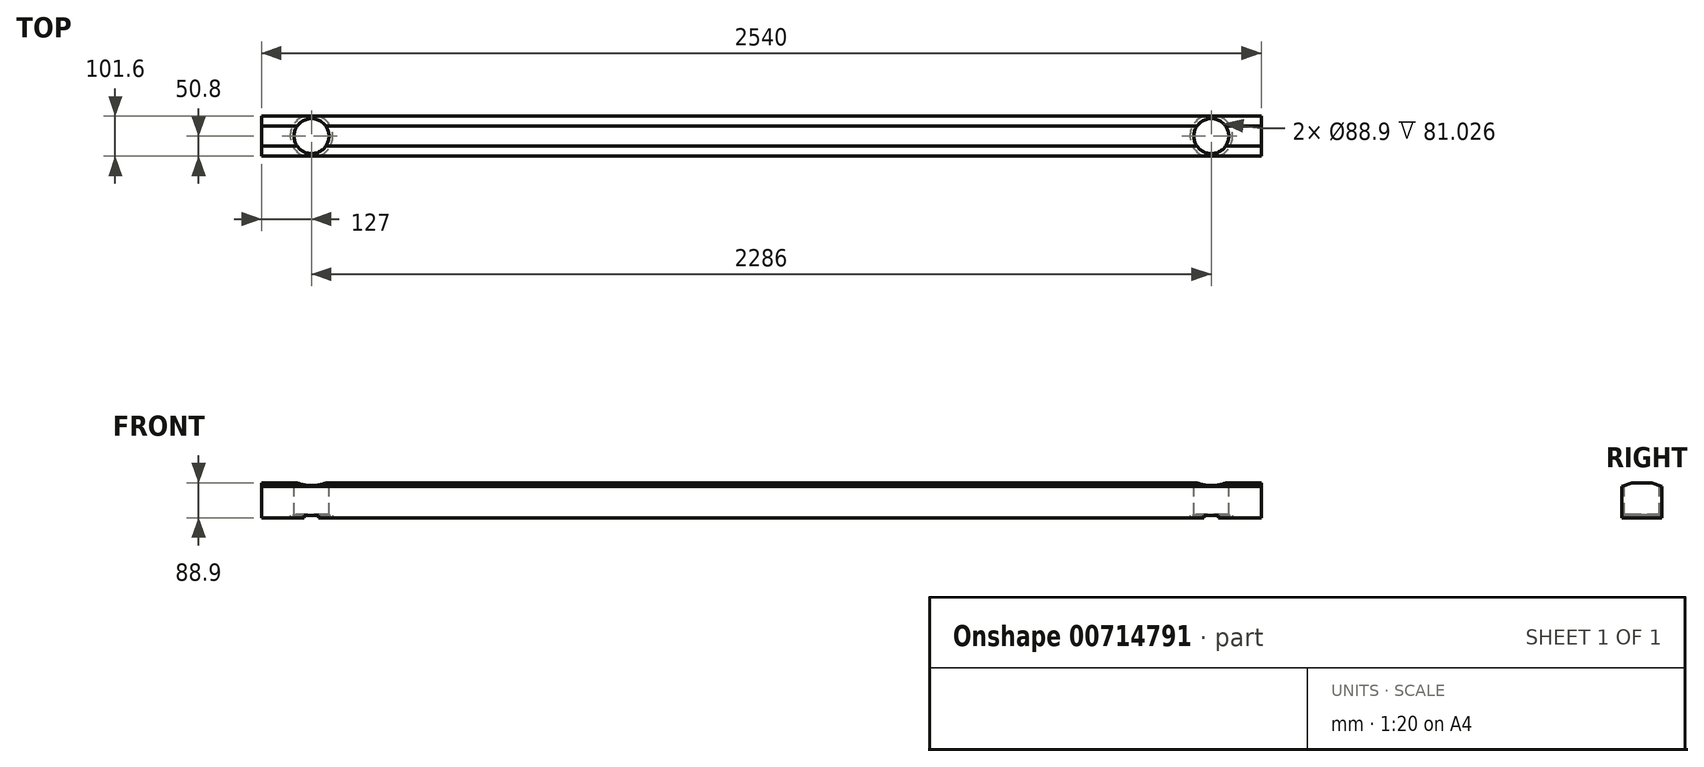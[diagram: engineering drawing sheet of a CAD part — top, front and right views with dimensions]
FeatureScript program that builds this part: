
annotation { "Feature Type Name" : "Feature", "Feature Type Description" : "" }
export const myFeature = defineFeature(function(context is Context, id is Id, definition is map)
    precondition{}
    {
        {
            var Q0;
            Q0=qCreatedBy(makeId("Right.planeOp"),FACE);
            var sketch = newSketch(context, id + "F0", { "sketchPlane" : qUnion([Q0])});
            skLineSegment(sketch, "E0", {"start": v(-25.4, 0) * mm, "end": v(25.4, 0) * mm});
            skLineSegment(sketch, "E1", {"start": v(25.4, 0) * mm, "end": v(50.8, -9.24) * mm});
            skLineSegment(sketch, "E2", {"start": v(-25.4, 0) * mm, "end": v(-50.8, -9.24) * mm});
            skLineSegment(sketch, "E3", {"start": v(-50.8, -9.24) * mm, "end": v(-50.8, -88.9) * mm});
            skLineSegment(sketch, "E4", {"start": v(-50.8, -88.9) * mm, "end": v(50.8, -88.9) * mm});
            skLineSegment(sketch, "E5", {"start": v(50.8, -88.9) * mm, "end": v(50.8, -9.24) * mm});
            skSolve(sketch);
        }
        {
            var Q0;
            Q0 = qSketchRegion(id + "F0", true);
            extrude(context, id + "F1", {"entities" : qUnion([Q0]), "endBound" : BoundingType.SYMMETRIC, "depth" : 2540 * mm, "offsetDistance" : 25.4 * mm});
        }
        {
            var Q0;
            Q0=qCreatedBy(makeId("Top.planeOp"),FACE);
            var sketch = newSketch(context, id + "F2", { "sketchPlane" : qUnion([Q0])});
            skCircle(sketch, "E6", {"center": v(1143, 0) * mm, "radius": 44.45 * mm});
            skCircle(sketch, "E7.MirrorC", {"center": v(-1143, 0) * mm, "radius": 44.45 * mm});
            skSolve(sketch);
        }
        {
            var Q0;
            Q0 = qSketchRegion(id + "F2", true);
            extrude(context, id + "F3", {"entities" : qUnion([Q0]), "operationType" : NewBodyOperationType.REMOVE, "endBound" : BoundingType.THROUGH_ALL, "oppositeDirection" : true, "depth" : 25.4 * mm, "offsetDistance" : 25.4 * mm});
        }
        {
            var Q0;
            Q0=makeQuery(id+"F1.opExtrude","SWEPT_FACE",FACE,{"disambiguationData":[OSD([sQuery(id+"F0.wireOp",EDGE,"E4")])]});
            var sketch = newSketch(context, id + "F4", { "sketchPlane" : qUnion([Q0])});
            skCircle(sketch, "E8", {"center": v(1143, 0) * mm, "radius": 54.04 * mm});
            skCircle(sketch, "E9.MirrorC", {"center": v(-1143, 0) * mm, "radius": 54.04 * mm});
            skSolve(sketch);
        }
        {
            var Q0;
            Q0 = qSketchRegion(id + "F4", true);
            extrude(context, id + "F5", {"entities" : qUnion([Q0]), "operationType" : NewBodyOperationType.REMOVE, "oppositeDirection" : true, "depth" : 6.35 * mm, "offsetDistance" : 25.4 * mm});
        }
        {
            var Q0;
            Q0=makeQuery(id+"F5.boolean.opBoolean","INTERSECT",EDGE,{"derivedFrom":[makeQuery(id+"F3.boolean.opBoolean","COPY",FACE,{"derivedFrom":makeQuery(id+"F3.opExtrude","SWEPT_FACE",FACE,{"disambiguationData":[OSD([sQuery(id+"F2.wireOp",EDGE,"E6")])]})}),makeQuery(id+"F5.opExtrude","CAP_FACE",FACE,{"disambiguationData":[OSD([sQuery(id+"F4.wireOp",EDGE,"E8")])],"isStart":false})]});
            chamfer(context, id + "F6", {"entities" : qUnion([Q0]), "width" : 1.52 * mm, "tangentPropagation" : true});
        }
        {
            var Q0;
            Q0=makeQuery(id+"F5.boolean.opBoolean","INTERSECT",EDGE,{"derivedFrom":[makeQuery(id+"F3.boolean.opBoolean","COPY",FACE,{"derivedFrom":makeQuery(id+"F3.opExtrude","SWEPT_FACE",FACE,{"disambiguationData":[OSD([sQuery(id+"F2.wireOp",EDGE,"E7.MirrorC")])]})}),makeQuery(id+"F5.opExtrude","CAP_FACE",FACE,{"disambiguationData":[OSD([sQuery(id+"F4.wireOp",EDGE,"E9.MirrorC")])],"isStart":false})]});
            chamfer(context, id + "F7", {"entities" : qUnion([Q0]), "width" : 1.52 * mm, "tangentPropagation" : true});
        }
    });
